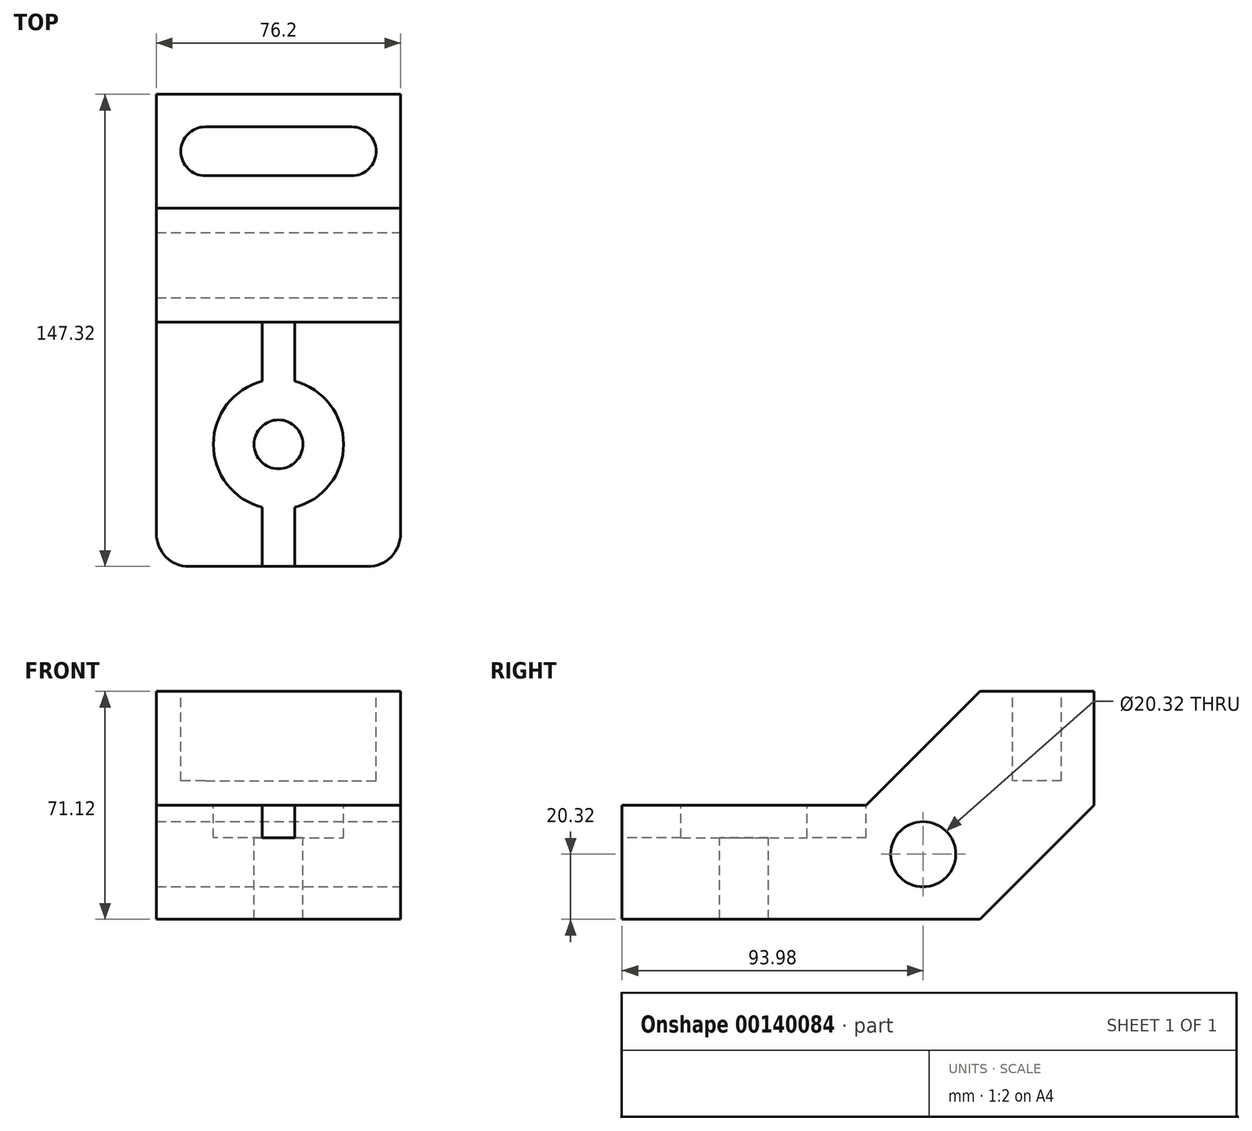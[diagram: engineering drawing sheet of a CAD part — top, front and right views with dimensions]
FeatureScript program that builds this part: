
annotation { "Feature Type Name" : "Feature", "Feature Type Description" : "" }
export const myFeature = defineFeature(function(context is Context, id is Id, definition is map)
    precondition{}
    {
        {
            var Q0;
            Q0=qCreatedBy(makeId("Right.planeOp"),FACE);
            var sketch = newSketch(context, id + "F0", { "sketchPlane" : qUnion([Q0])});
            skLineSegment(sketch, "E0", {"start": v(0, 0) * mm, "end": v(35.56, 35.56) * mm});
            skLineSegment(sketch, "E1", {"start": v(35.56, 35.56) * mm, "end": v(35.56, 71.12) * mm});
            skLineSegment(sketch, "E2", {"start": v(35.56, 71.12) * mm, "end": v(0, 71.12) * mm});
            skLineSegment(sketch, "E3", {"start": v(0, 71.12) * mm, "end": v(-35.56, 35.56) * mm});
            skLineSegment(sketch, "E4", {"start": v(-35.56, 35.56) * mm, "end": v(-111.76, 35.56) * mm});
            skLineSegment(sketch, "E5", {"start": v(-111.76, 35.56) * mm, "end": v(-111.76, 0) * mm});
            skLineSegment(sketch, "E6", {"start": v(-111.76, 0) * mm, "end": v(0, 0) * mm});
            skSolve(sketch);
        }
        {
            var Q0;
            Q0 = qSketchRegion(id + "F0", true);
            extrude(context, id + "F1", {"entities" : qUnion([Q0]), "endBound" : BoundingType.SYMMETRIC, "depth" : 76.2 * mm});
        }
        {
            var Q0;
            Q0=makeQuery(id+"F1.opExtrude","CAP_FACE",FACE,{"disambiguationData":[OSD([sQuery(id+"F0.wireOp",EDGE,"E0"),sQuery(id+"F0.wireOp",EDGE,"E1"),sQuery(id+"F0.wireOp",EDGE,"E2"),sQuery(id+"F0.wireOp",EDGE,"E3"),sQuery(id+"F0.wireOp",EDGE,"E4"),sQuery(id+"F0.wireOp",EDGE,"E5"),sQuery(id+"F0.wireOp",EDGE,"E6")])],"isStart":false});
            var sketch = newSketch(context, id + "F2", { "sketchPlane" : qUnion([Q0])});
            skLineSegment(sketch, "E7", {"start": v(35.56, 35.56) * mm, "end": v(-17.78, 35.56) * mm, "construction": true});
            skLineSegment(sketch, "E8", {"start": v(-17.78, 35.56) * mm, "end": v(-17.78, 20.32) * mm, "construction": true});
            skLineSegment(sketch, "E9", {"start": v(-17.78, 20.32) * mm, "end": v(-17.78, 0) * mm, "construction": true});
            skSolve(sketch);
        }
        {
            var Q0;
            Q0=sQuery(id+"F2.wireOp",VERTEX,"E9.start");
            var Q1;
            Q1=makeQuery(id+"F1.opExtrude","SWEPT_BODY",BODY,{"disambiguationData":[OSD([sQuery(id+"F0.wireOp",EDGE,"E0"),sQuery(id+"F0.wireOp",EDGE,"E1"),sQuery(id+"F0.wireOp",EDGE,"E2"),sQuery(id+"F0.wireOp",EDGE,"E3"),sQuery(id+"F0.wireOp",EDGE,"E4"),sQuery(id+"F0.wireOp",EDGE,"E5"),sQuery(id+"F0.wireOp",EDGE,"E6")])]});
            hole(context, id + "F3", {"style" : HoleStyle.SIMPLE, "endStyle" : HoleEndStyle.THROUGH, "holeDiameter" : 20.32 * mm, "locations" : qUnion([Q0]), "scope" : qUnion([Q1]), "isTappedThrough" : true});
        }
        {
            var Q0;
            Q0=makeQuery(id+"F1.opExtrude","SWEPT_FACE",FACE,{"disambiguationData":[OSD([sQuery(id+"F0.wireOp",EDGE,"E2")])]});
            var sketch = newSketch(context, id + "F4", { "sketchPlane" : qUnion([Q0])});
            skArc(sketch, "E10", {"start": v(22.86, 10.16) * mm, "mid": v(30.48, 17.78) * mm, "end": v(22.86, 25.4) * mm});
            skArc(sketch, "E11", {"start": v(-22.86, 10.16) * mm, "mid": v(-30.48, 17.78) * mm, "end": v(-22.86, 25.4) * mm});
            skLineSegment(sketch, "E12", {"start": v(-22.86, 25.4) * mm, "end": v(22.86, 25.4) * mm});
            skLineSegment(sketch, "E13", {"start": v(22.86, 10.16) * mm, "end": v(-22.86, 10.16) * mm});
            skSolve(sketch);
        }
        {
            var Q0;
            Q0=makeQuery(id+"F4.imprint","IMPRINT",FACE,{"disambiguationData":[TD([[makeQuery(id+"F4.imprint","IMPRINT",EDGE,{"derivedFrom":sQuery(id+"F4.wireOp",EDGE,"E10")}),1.0]])]});
            extrude(context, id + "F5", {"entities" : qUnion([Q0]), "operationType" : NewBodyOperationType.REMOVE, "oppositeDirection" : true, "depth" : 27.94 * mm});
        }
        {
            var Q0;
            Q0=makeQuery(id+"F1.opExtrude","SWEPT_FACE",FACE,{"disambiguationData":[OSD([sQuery(id+"F0.wireOp",EDGE,"E4")])]});
            var sketch = newSketch(context, id + "F6", { "sketchPlane" : qUnion([Q0])});
            skLineSegment(sketch, "E14", {"start": v(0, -111.76) * mm, "end": v(0, -73.66) * mm, "construction": true});
            skPoint(sketch, "E14.endSnap0", {"position": v(0, -111.76) * mm});
            skSolve(sketch);
        }
        {
            var Q0;
            Q0=sQuery(id+"F6.wireOp",VERTEX,"E14.end");
            var Q1;
            Q1=makeQuery(id+"F1.opExtrude","SWEPT_BODY",BODY,{"disambiguationData":[OSD([sQuery(id+"F0.wireOp",EDGE,"E0"),sQuery(id+"F0.wireOp",EDGE,"E1"),sQuery(id+"F0.wireOp",EDGE,"E2"),sQuery(id+"F0.wireOp",EDGE,"E3"),sQuery(id+"F0.wireOp",EDGE,"E4"),sQuery(id+"F0.wireOp",EDGE,"E5"),sQuery(id+"F0.wireOp",EDGE,"E6")])]});
            hole(context, id + "F7", {"style" : HoleStyle.C_BORE, "endStyle" : HoleEndStyle.THROUGH, "holeDiameter" : 15.24 * mm, "cBoreDiameter" : 40.64 * mm, "cBoreDepth" : 10.16 * mm, "locations" : qUnion([Q0]), "scope" : qUnion([Q1]), "isTappedThrough" : true});
        }
        {
            var Q0;
            Q0=makeQuery(id+"F1.opExtrude","SWEPT_FACE",FACE,{"disambiguationData":[OSD([sQuery(id+"F0.wireOp",EDGE,"E5")])]});
            var sketch = newSketch(context, id + "F8", { "sketchPlane" : qUnion([Q0])});
            skLineSegment(sketch, "E15", {"start": v(0, 35.56) * mm, "end": v(5.08, 35.56) * mm});
            skLineSegment(sketch, "E16", {"start": v(5.08, 35.56) * mm, "end": v(5.08, 25.4) * mm});
            skLineSegment(sketch, "E17", {"start": v(5.08, 25.4) * mm, "end": v(-5.08, 25.4) * mm});
            skLineSegment(sketch, "E18", {"start": v(-5.08, 25.4) * mm, "end": v(-5.08, 35.56) * mm});
            skLineSegment(sketch, "E19", {"start": v(-5.08, 35.56) * mm, "end": v(0, 35.56) * mm});
            skSolve(sketch);
        }
        {
            var Q0;
            Q0=makeQuery(id+"F8.imprint","IMPRINT",FACE,{"disambiguationData":[TD([[makeQuery(id+"F8.imprint","IMPRINT",EDGE,{"derivedFrom":sQuery(id+"F8.wireOp",EDGE,"E15")}),1.0]])]});
            extrude(context, id + "F9", {"entities" : qUnion([Q0]), "operationType" : NewBodyOperationType.REMOVE, "oppositeDirection" : true, "depth" : 76.2 * mm});
        }
        {
            var Q0;
            Q0=makeQuery(id+"F1.opExtrude","CAP_EDGE",EDGE,{"disambiguationData":[OSD([sQuery(id+"F0.wireOp",EDGE,"E5")])],"isStart":true});
            var Q1;
            Q1=makeQuery(id+"F1.opExtrude","CAP_EDGE",EDGE,{"disambiguationData":[OSD([sQuery(id+"F0.wireOp",EDGE,"E5")])],"isStart":false});
            fillet(context, id + "F10", {"entities" : qUnion([Q0, Q1]), "radius" : 10.16 * mm, "tangentPropagation" : true, "allowEdgeOverflow" : false});
        }
    });
